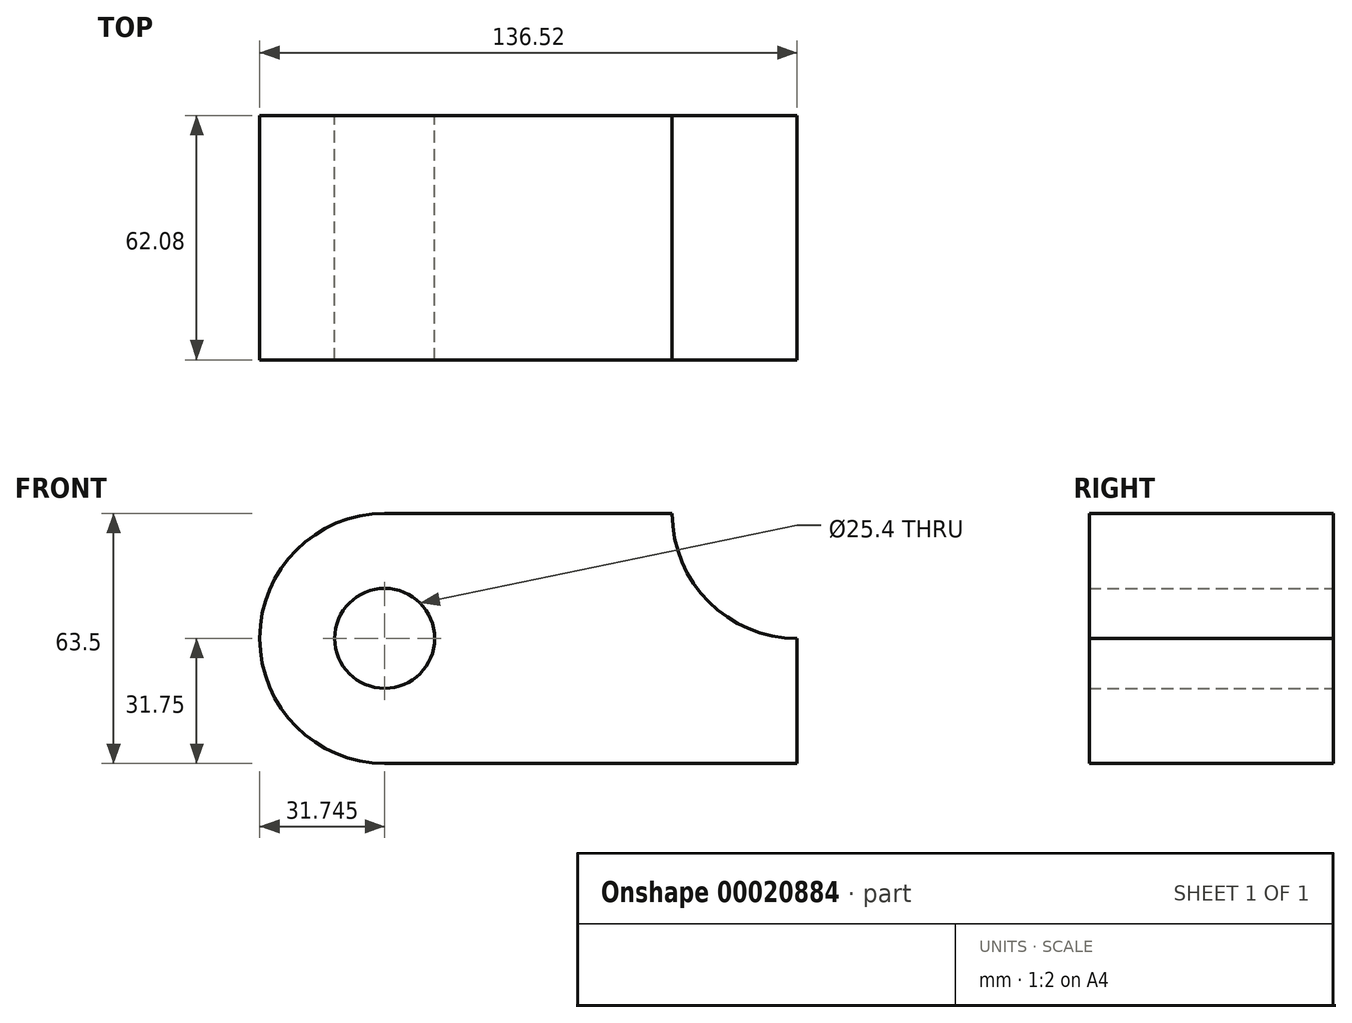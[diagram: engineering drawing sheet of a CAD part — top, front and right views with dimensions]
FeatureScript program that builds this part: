
annotation { "Feature Type Name" : "Feature", "Feature Type Description" : "" }
export const myFeature = defineFeature(function(context is Context, id is Id, definition is map)
    precondition{}
    {
        {
            var Q0;
            Q0=qCreatedBy(makeId("Front.planeOp"),FACE);
            var sketch = newSketch(context, id + "F0", { "sketchPlane" : qUnion([Q0])});
            skLineSegment(sketch, "E0.bottom", {"start": v(-31.75, 0) * mm, "end": v(-104.78, 0) * mm});
            skLineSegment(sketch, "E0.top", {"start": v(0, -63.5) * mm, "end": v(-104.77, -63.5) * mm});
            skLineSegment(sketch, "E0.left", {"start": v(0, -31.75) * mm, "end": v(0, -63.5) * mm});
            skArc(sketch, "E1", {"start": v(-104.77, 0) * mm, "mid": v(-136.53, -31.75) * mm, "end": v(-104.77, -63.5) * mm});
            skCircle(sketch, "E2", {"center": v(-104.77, -31.75) * mm, "radius": 12.7 * mm});
            skArc(sketch, "E3", {"start": v(-31.75, 0) * mm, "mid": v(-22.45, -22.45) * mm, "end": v(0, -31.75) * mm});
            skSolve(sketch);
        }
        {
            var Q0;
            Q0=makeQuery(id+"F0.imprint","IMPRINT",FACE,{"disambiguationData":[TD([[makeQuery(id+"F0.imprint","IMPRINT",EDGE,{"derivedFrom":sQuery(id+"F0.wireOp",EDGE,"E0.bottom")}),1.0]])]});
            extrude(context, id + "F1", {"entities" : qUnion([Q0]), "depth" : 62.08 * mm});
        }
    });
